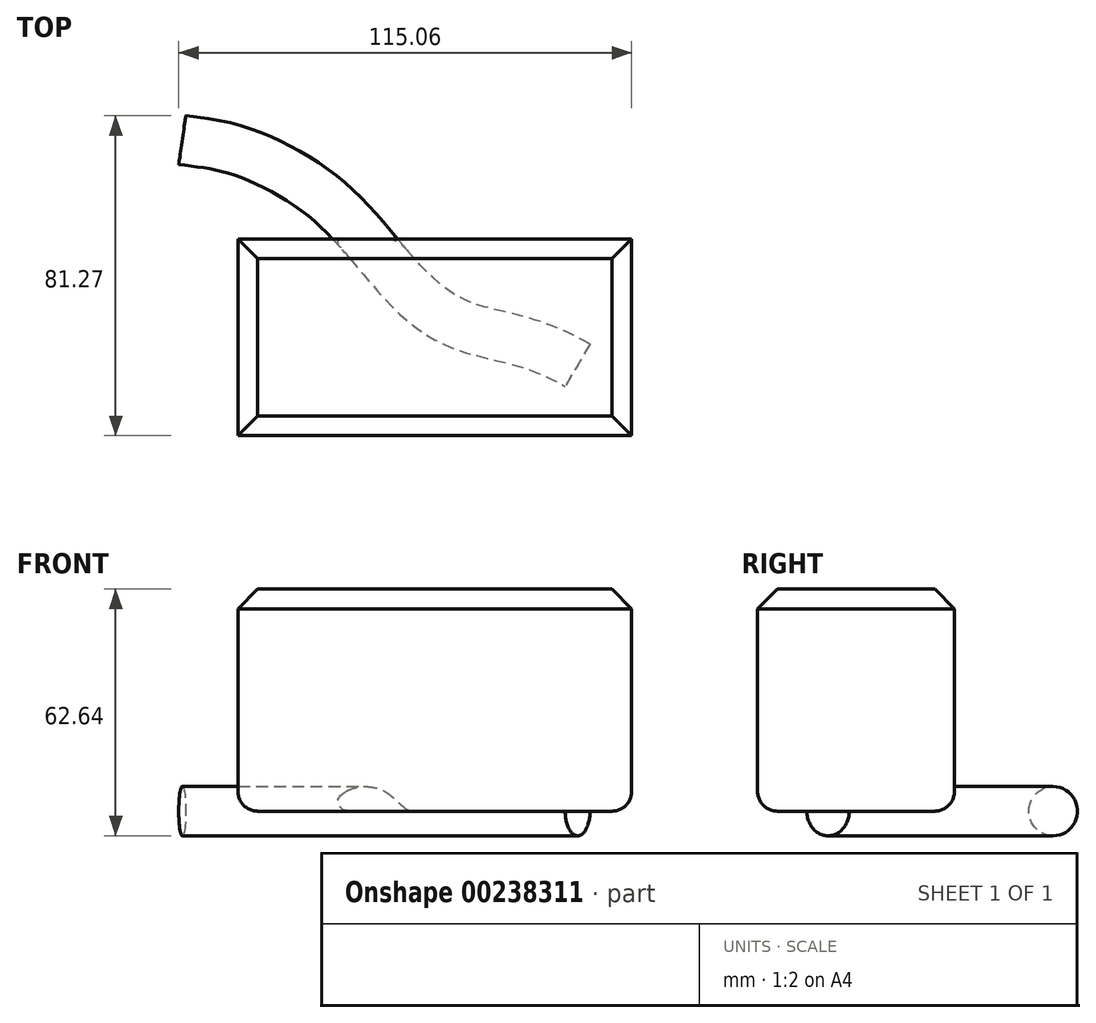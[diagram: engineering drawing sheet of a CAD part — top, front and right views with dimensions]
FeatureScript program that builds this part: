
annotation { "Feature Type Name" : "Feature", "Feature Type Description" : "" }
export const myFeature = defineFeature(function(context is Context, id is Id, definition is map)
    precondition{}
    {
        {
            var Q0;
            Q0=qCreatedBy(makeId("Top.planeOp"),FACE);
            var sketch = newSketch(context, id + "F0", { "sketchPlane" : qUnion([Q0])});
            skLineSegment(sketch, "E0.bottom", {"start": v(0, 0) * mm, "end": v(100, 0) * mm});
            skLineSegment(sketch, "E0.top", {"start": v(0, -50) * mm, "end": v(100, -50) * mm});
            skLineSegment(sketch, "E0.left", {"start": v(0, 0) * mm, "end": v(0, -50) * mm});
            skLineSegment(sketch, "E0.right", {"start": v(100, 0) * mm, "end": v(100, -50) * mm});
            skSolve(sketch);
        }
        {
            var Q0;
            Q0=makeQuery(id+"F0.imprint","IMPRINT",FACE,{"disambiguationData":[TD([[makeQuery(id+"F0.imprint","IMPRINT",EDGE,{"derivedFrom":sQuery(id+"F0.wireOp",EDGE,"E0.bottom")}),-1.0]])]});
            extrude(context, id + "F1", {"entities" : qUnion([Q0]), "depth" : 56.4 * mm});
        }
        {
            var Q0;
            Q0=makeQuery(id+"F1.opExtrude","CAP_EDGE",EDGE,{"disambiguationData":[OSD([sQuery(id+"F0.wireOp",EDGE,"E0.top")])],"isStart":false});
            var Q1;
            Q1=makeQuery(id+"F1.opExtrude","CAP_EDGE",EDGE,{"disambiguationData":[OSD([sQuery(id+"F0.wireOp",EDGE,"E0.right")])],"isStart":false});
            var Q2;
            Q2=makeQuery(id+"F1.opExtrude","CAP_EDGE",EDGE,{"disambiguationData":[OSD([sQuery(id+"F0.wireOp",EDGE,"E0.bottom")])],"isStart":false});
            var Q3;
            Q3=makeQuery(id+"F1.opExtrude","CAP_EDGE",EDGE,{"disambiguationData":[OSD([sQuery(id+"F0.wireOp",EDGE,"E0.left")])],"isStart":false});
            chamfer(context, id + "F2", {"entities" : qUnion([Q0, Q1, Q2, Q3]), "width" : 5 * mm, "tangentPropagation" : true});
        }
        {
            var Q0;
            Q0=makeQuery(id+"F1.opExtrude","CAP_EDGE",EDGE,{"disambiguationData":[OSD([sQuery(id+"F0.wireOp",EDGE,"E0.top")])],"isStart":true});
            var Q1;
            Q1=makeQuery(id+"F1.opExtrude","CAP_EDGE",EDGE,{"disambiguationData":[OSD([sQuery(id+"F0.wireOp",EDGE,"E0.right")])],"isStart":true});
            var Q2;
            Q2=makeQuery(id+"F1.opExtrude","CAP_EDGE",EDGE,{"disambiguationData":[OSD([sQuery(id+"F0.wireOp",EDGE,"E0.bottom")])],"isStart":true});
            var Q3;
            Q3=makeQuery(id+"F1.opExtrude","CAP_EDGE",EDGE,{"disambiguationData":[OSD([sQuery(id+"F0.wireOp",EDGE,"E0.left")])],"isStart":true});
            fillet(context, id + "F3", {"entities" : qUnion([Q0, Q1, Q2, Q3]), "radius" : 5 * mm, "tangentPropagation" : true, "allowEdgeOverflow" : false});
        }
        {
            var Q0;
            Q0=qCreatedBy(makeId("Top.planeOp"),FACE);
            var sketch = newSketch(context, id + "F4", { "sketchPlane" : qUnion([Q0])});
            skFitSpline(sketch, "E1", {"points": [v(86.28, -32.1) * mm, v(56.51, -21.8) * mm, v(40.27, -9.28) * mm, v(23.24, 9.44) * mm, v(0, 22.48) * mm, v(-14.16, 25.1) * mm], "startDerivative": vector(-157.96, 92.45) * mm, "endDerivative": vector(-80.74, 11.8) * mm});
            skSolve(sketch);
        }
        {
            var Q0;
            Q0=sQuery(id+"F4.wireOp",EDGE,"E1");
            var Q1;
            Q1=sQuery(id+"F4.wireOp",VERTEX,"E1.end");
            cPlane(context, id + "F5", {"entities" : qUnion([Q0, Q1]), "cplaneType" : CPlaneType.CURVE_POINT, "offset" : 25 * mm, "width" : 150 * mm, "height" : 150 * mm});
        }
        {
            var Q0;
            Q0=qCreatedBy(id+"F5.planeOp",FACE);
            var sketch = newSketch(context, id + "F6", { "sketchPlane" : qUnion([Q0])});
            skCircle(sketch, "E2", {"center": v(-22.78, 0) * mm, "radius": 6.24 * mm});
            skSolve(sketch);
        }
        {
            var Q0;
            Q0=makeQuery(id+"F6.imprint","IMPRINT",FACE,{"disambiguationData":[TD([[makeQuery(id+"F6.imprint","IMPRINT",EDGE,{"derivedFrom":sQuery(id+"F6.wireOp",EDGE,"E2")}),1.0]])]});
            var Q1;
            Q1=sQuery(id+"F4.wireOp",EDGE,"E1");
            sweep(context, id + "F7", {"operationType" : NewBodyOperationType.ADD, "profiles" : qUnion([Q0]), "path" : qUnion([Q1])});
        }
    });
